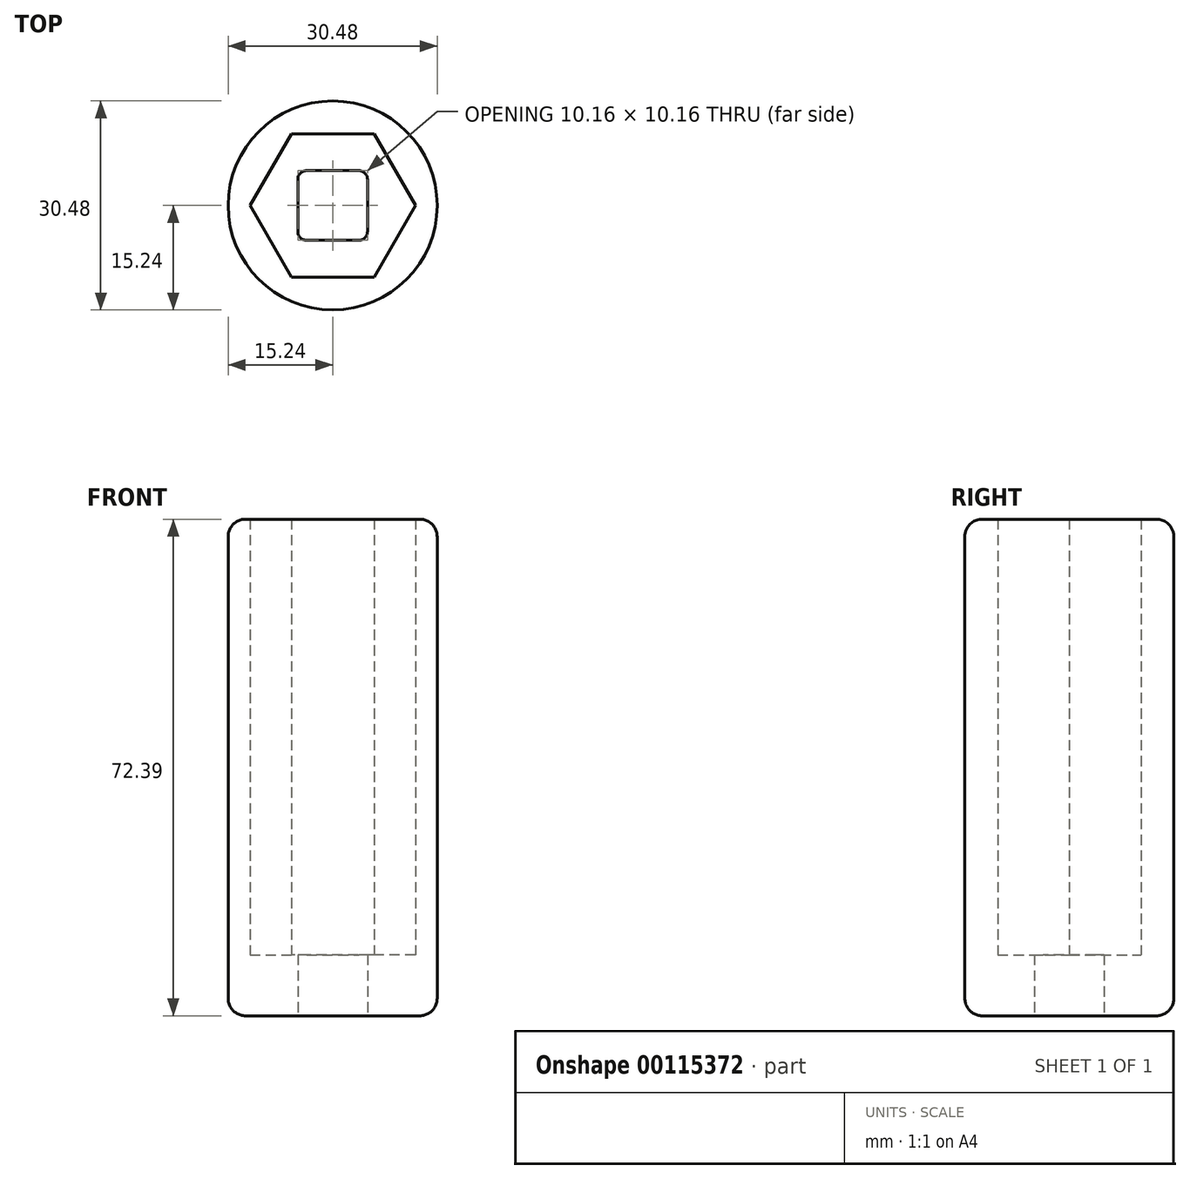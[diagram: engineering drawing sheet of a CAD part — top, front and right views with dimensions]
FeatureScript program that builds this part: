
annotation { "Feature Type Name" : "Feature", "Feature Type Description" : "" }
export const myFeature = defineFeature(function(context is Context, id is Id, definition is map)
    precondition{}
    {
        {
            var Q0;
            Q0=qCreatedBy(makeId("Top.planeOp"),FACE);
            var sketch = newSketch(context, id + "F0", { "sketchPlane" : qUnion([Q0])});
            skCircle(sketch, "E0", {"center": v(0, 0) * mm, "radius": 15.24 * mm});
            skLineSegment(sketch, "E1.bottom", {"start": v(-5.08, 5.08) * mm, "end": v(5.08, 5.08) * mm});
            skLineSegment(sketch, "E1.top", {"start": v(-5.08, -5.08) * mm, "end": v(5.08, -5.08) * mm});
            skLineSegment(sketch, "E1.left", {"start": v(-5.08, 5.08) * mm, "end": v(-5.08, -5.08) * mm});
            skLineSegment(sketch, "E1.right", {"start": v(5.08, 5.08) * mm, "end": v(5.08, -5.08) * mm});
            skSolve(sketch);
        }
        {
            var Q0;
            Q0 = qSketchRegion(id + "F0", true);
            extrude(context, id + "F1", {"entities" : qUnion([Q0]), "depth" : 8.9 * mm});
        }
        {
            var Q0;
            Q0=makeQuery(id+"F1.opExtrude","CAP_FACE",FACE,{"disambiguationData":[OSD([sQuery(id+"F0.wireOp",EDGE,"E0"),sQuery(id+"F0.wireOp",EDGE,"E1.bottom"),sQuery(id+"F0.wireOp",EDGE,"E1.top"),sQuery(id+"F0.wireOp",EDGE,"E1.left"),sQuery(id+"F0.wireOp",EDGE,"E1.right")])],"isStart":false});
            var sketch = newSketch(context, id + "F2", { "sketchPlane" : qUnion([Q0])});
            skCircle(sketch, "E2", {"center": v(0, 0) * mm, "radius": 15.24 * mm});
            skCircle(sketch, "E3.cCircle", {"center": v(0, 0) * mm, "radius": 12.07 * mm, "construction": true});
            skLineSegment(sketch, "E3.0", {"start": v(-6.03, 10.45) * mm, "end": v(6.03, 10.45) * mm});
            skLineSegment(sketch, "E3.1", {"start": v(6.03, 10.45) * mm, "end": v(12.07, 0) * mm});
            skLineSegment(sketch, "E3.2", {"start": v(12.07, 0) * mm, "end": v(6.03, -10.45) * mm});
            skLineSegment(sketch, "E3.3", {"start": v(6.03, -10.45) * mm, "end": v(-6.03, -10.45) * mm});
            skLineSegment(sketch, "E3.4", {"start": v(-6.03, -10.45) * mm, "end": v(-12.07, 0) * mm});
            skLineSegment(sketch, "E3.5", {"start": v(-12.07, 0) * mm, "end": v(-6.03, 10.45) * mm});
            skSolve(sketch);
        }
        {
            var Q0;
            Q0 = qSketchRegion(id + "F2", true);
            extrude(context, id + "F3", {"entities" : qUnion([Q0]), "operationType" : NewBodyOperationType.ADD, "depth" : 63.5 * mm});
        }
        {
            var Q0;
            Q0=makeQuery(id+"F1.opExtrude","SWEPT_EDGE",EDGE,{"disambiguationData":[OSD([sQuery(id+"F0.wireOp",EDGE,"E1.top"),sQuery(id+"F0.wireOp",EDGE,"E1.left")])]});
            var Q1;
            Q1=makeQuery(id+"F1.opExtrude","SWEPT_EDGE",EDGE,{"disambiguationData":[OSD([sQuery(id+"F0.wireOp",EDGE,"E1.bottom"),sQuery(id+"F0.wireOp",EDGE,"E1.left")])]});
            var Q2;
            Q2=makeQuery(id+"F1.opExtrude","SWEPT_EDGE",EDGE,{"disambiguationData":[OSD([sQuery(id+"F0.wireOp",EDGE,"E1.top"),sQuery(id+"F0.wireOp",EDGE,"E1.right")])]});
            var Q3;
            Q3=makeQuery(id+"F1.opExtrude","SWEPT_EDGE",EDGE,{"disambiguationData":[OSD([sQuery(id+"F0.wireOp",EDGE,"E1.bottom"),sQuery(id+"F0.wireOp",EDGE,"E1.right")])]});
            fillet(context, id + "F4", {"entities" : qUnion([Q0, Q1, Q2, Q3]), "radius" : 1.27 * mm, "tangentPropagation" : true, "allowEdgeOverflow" : false});
        }
        {
            var Q0;
            Q0=makeQuery(id+"F1.opExtrude","CAP_EDGE",EDGE,{"disambiguationData":[OSD([sQuery(id+"F0.wireOp",EDGE,"E0")])],"isStart":true});
            var Q1;
            Q1=makeQuery(id+"F3.opExtrude","CAP_EDGE",EDGE,{"disambiguationData":[OSD([sQuery(id+"F2.wireOp",EDGE,"E2")])],"isStart":false});
            fillet(context, id + "F5", {"entities" : qUnion([Q0, Q1]), "radius" : 2.54 * mm, "tangentPropagation" : true, "allowEdgeOverflow" : false});
        }
    });
